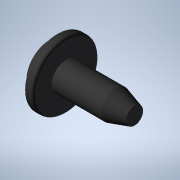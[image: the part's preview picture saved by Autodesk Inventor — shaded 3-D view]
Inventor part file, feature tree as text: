
AUTODESK INVENTOR PART (.ipt)
format: ipt  version: 2021 (Build 250183000, 183)  size: 155,648 bytes
history: native  units: mm
features: other x7, revolve x1, sketch x1
ambient origin geometry x8: Origin, YZ Plane, XZ Plane, XY Plane, X Axis, Y Axis, Z Axis, Center Point
bodies: Solid1 (feature_tree)
feature tree (9):
  revolve  "Revolution1"  [1 undecoded]
  other  "SCHRAUBE_XY"
  other  "SCHRAUBE_YZ"
  other  "SCHRAUBE_ZX"
  other  "SCHRAUBE_X"
  other  "SCHRAUBE_Y"
  other  "SCHRAUBE_Z"
  other  "SCHRAUBE_Center"
  sketch  "Sketch_1"  dims[d0=360.0deg d1=0.0mm]
note: 1 required parameter value undecoded (feature->parameter linkage not recoverable at this tier; creation-order binding heuristic only, values carry confidence <= 0.55)
